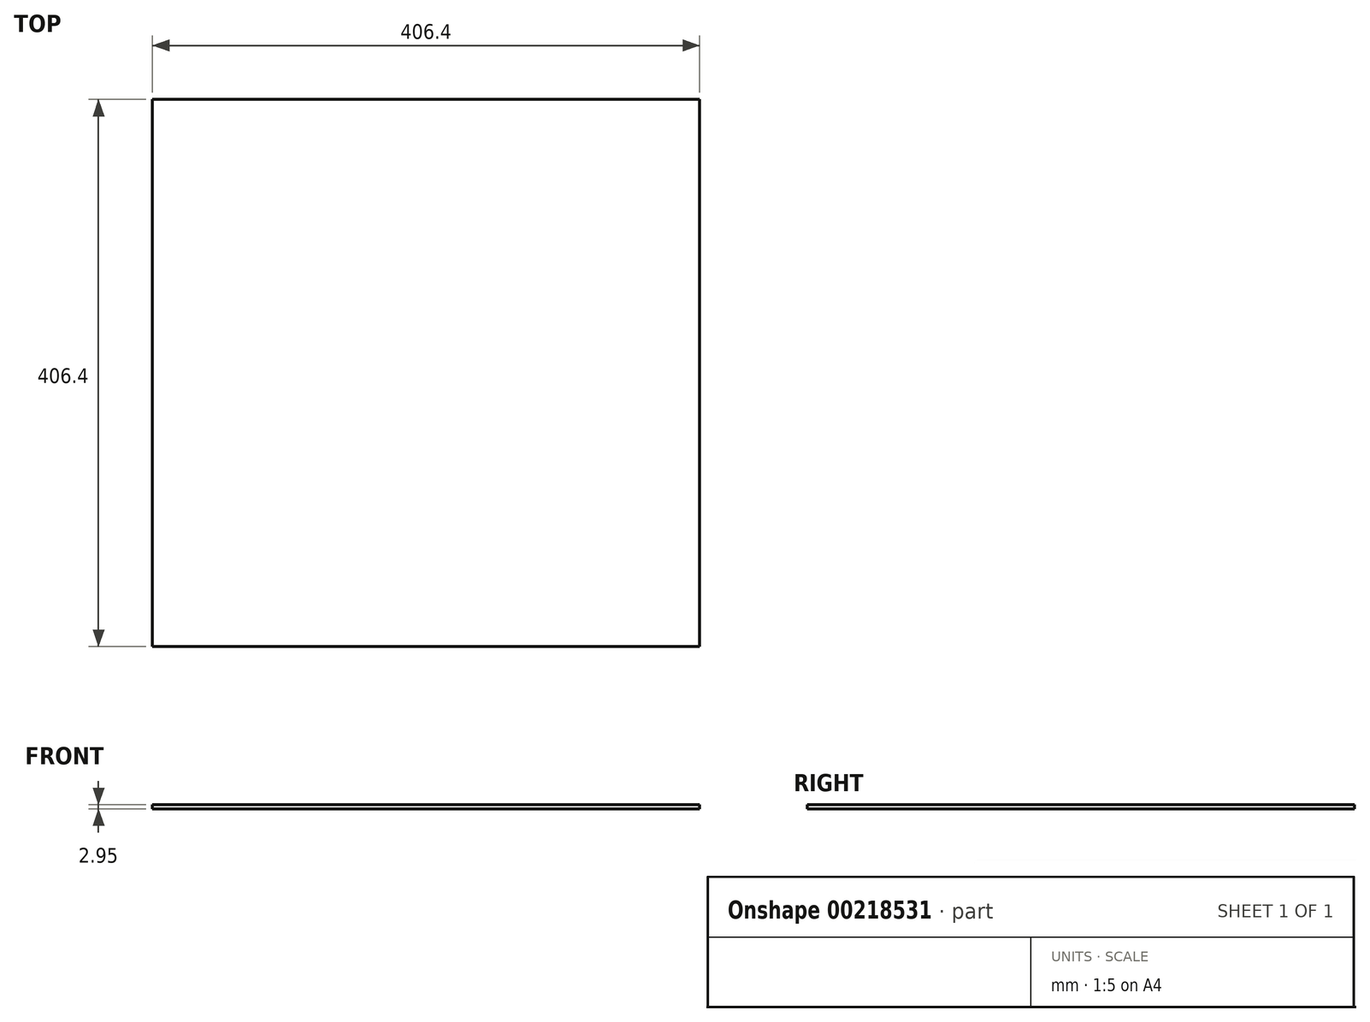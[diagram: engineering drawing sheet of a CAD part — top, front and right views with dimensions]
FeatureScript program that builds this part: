
annotation { "Feature Type Name" : "Feature", "Feature Type Description" : "" }
export const myFeature = defineFeature(function(context is Context, id is Id, definition is map)
    precondition{}
    {
        {
            assignVariable(context, id + "F0", {"name" : "THK", "anyValue" : 2.95 * mm});
        }
        {
            var Q0;
            Q0=qCreatedBy(makeId("Top.planeOp"),FACE);
            var sketch = newSketch(context, id + "F1", { "sketchPlane" : qUnion([Q0])});
            skLineSegment(sketch, "E0.bottom", {"start": v(187.18, 197.96) * mm, "end": v(-219.22, 197.96) * mm});
            skLineSegment(sketch, "E0.top", {"start": v(187.18, -208.44) * mm, "end": v(-219.22, -208.44) * mm});
            skLineSegment(sketch, "E0.left", {"start": v(187.18, 197.96) * mm, "end": v(187.18, -208.44) * mm});
            skLineSegment(sketch, "E0.right", {"start": v(-219.22, 197.96) * mm, "end": v(-219.22, -208.44) * mm});
            skSolve(sketch);
        }
        {
            var Q0;
            Q0 = qSketchRegion(id + "F1", true);
            extrude(context, id + "F2", {"entities" : qUnion([Q0]), "depth" : getVariable(context, 'THK')});
        }
    });
